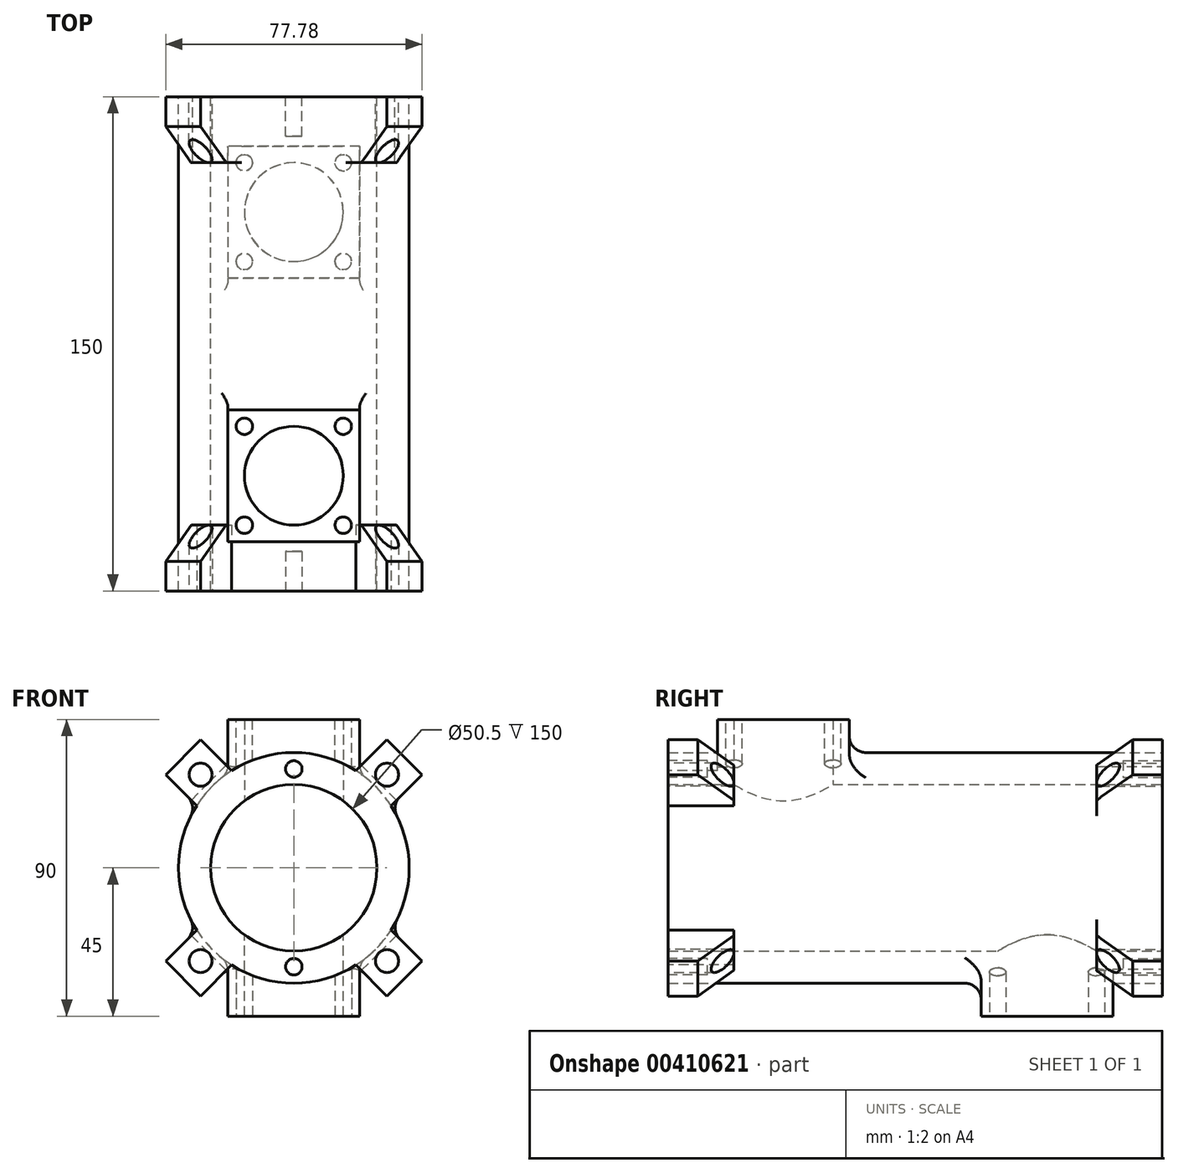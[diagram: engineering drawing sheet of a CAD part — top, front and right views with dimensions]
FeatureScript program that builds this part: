
annotation { "Feature Type Name" : "Feature", "Feature Type Description" : "" }
export const myFeature = defineFeature(function(context is Context, id is Id, definition is map)
    precondition{}
    {
        {
            var Q0;
            Q0=qCreatedBy(makeId("Front.planeOp"),FACE);
            var sketch = newSketch(context, id + "F0", { "sketchPlane" : qUnion([Q0])});
            skCircle(sketch, "E0", {"center": v(0, 0) * mm, "radius": 25.25 * mm});
            skCircle(sketch, "E1", {"center": v(0, 0) * mm, "radius": 35 * mm});
            skSolve(sketch);
        }
        {
            var Q0;
            Q0=makeQuery(id+"F0.imprint","IMPRINT",FACE,{"disambiguationData":[TD([[makeQuery(id+"F0.imprint","IMPRINT",EDGE,{"derivedFrom":sQuery(id+"F0.wireOp",EDGE,"E0")}),-1.0]])]});
            extrude(context, id + "F1", {"entities" : qUnion([Q0]), "depth" : 150 * mm});
        }
        {
            var Q0;
            Q0=qCreatedBy(makeId("Top.planeOp"),FACE);
            var sketch = newSketch(context, id + "F2", { "sketchPlane" : qUnion([Q0])});
            skCircle(sketch, "E2", {"center": v(0, -35) * mm, "radius": 15 * mm});
            skCircle(sketch, "E3", {"center": v(0, -115) * mm, "radius": 15 * mm});
            skSolve(sketch);
        }
        {
            var Q0;
            Q0=qCreatedBy(makeId("Top.planeOp"),FACE);
            cPlane(context, id + "F3", {"entities" : qUnion([Q0]), "cplaneType" : CPlaneType.OFFSET, "offset" : 45 * mm, "width" : 150 * mm, "height" : 150 * mm});
        }
        {
            var Q0;
            Q0=qCreatedBy(makeId("Top.planeOp"),FACE);
            cPlane(context, id + "F4", {"entities" : qUnion([Q0]), "cplaneType" : CPlaneType.OFFSET, "offset" : 45 * mm, "oppositeDirection" : true, "width" : 150 * mm, "height" : 150 * mm});
        }
        {
            var Q0;
            Q0=makeQuery(id+"F1.opExtrude","CAP_FACE",FACE,{"disambiguationData":[OSD([sQuery(id+"F0.wireOp",EDGE,"E0"),sQuery(id+"F0.wireOp",EDGE,"E1")])],"isStart":false});
            var sketch = newSketch(context, id + "F5", { "sketchPlane" : qUnion([Q0])});
            skLineSegment(sketch, "E4.bottom", {"start": v(-28.28, 17.68) * mm, "end": v(-38.9, 28.28) * mm});
            skLineSegment(sketch, "E4.top", {"start": v(-17.68, 28.28) * mm, "end": v(-28.28, 38.9) * mm});
            skLineSegment(sketch, "E4.left", {"start": v(-28.28, 17.68) * mm, "end": v(-17.68, 28.28) * mm});
            skLineSegment(sketch, "E4.right", {"start": v(-38.9, 28.28) * mm, "end": v(-28.28, 38.9) * mm});
            skPoint(sketch, "E4.middle", {"position": v(-28.28, 28.28) * mm});
            skLineSegment(sketch, "E5.bottom", {"start": v(28.28, 17.68) * mm, "end": v(17.68, 28.28) * mm});
            skLineSegment(sketch, "E5.top", {"start": v(38.9, 28.28) * mm, "end": v(28.28, 38.9) * mm});
            skLineSegment(sketch, "E5.left", {"start": v(28.28, 17.68) * mm, "end": v(38.9, 28.28) * mm});
            skLineSegment(sketch, "E5.right", {"start": v(17.68, 28.28) * mm, "end": v(28.28, 38.9) * mm});
            skPoint(sketch, "E5.middle", {"position": v(28.28, 28.28) * mm});
            skLineSegment(sketch, "E6.bottom", {"start": v(28.28, -38.9) * mm, "end": v(17.68, -28.28) * mm});
            skLineSegment(sketch, "E6.top", {"start": v(38.9, -28.28) * mm, "end": v(28.28, -17.68) * mm});
            skLineSegment(sketch, "E6.left", {"start": v(28.28, -38.9) * mm, "end": v(38.9, -28.28) * mm});
            skLineSegment(sketch, "E6.right", {"start": v(17.68, -28.28) * mm, "end": v(28.28, -17.68) * mm});
            skPoint(sketch, "E6.middle", {"position": v(28.28, -28.28) * mm});
            skLineSegment(sketch, "E7.bottom", {"start": v(-28.28, -38.9) * mm, "end": v(-38.9, -28.28) * mm});
            skLineSegment(sketch, "E7.top", {"start": v(-17.68, -28.28) * mm, "end": v(-28.28, -17.68) * mm});
            skLineSegment(sketch, "E7.left", {"start": v(-28.28, -38.9) * mm, "end": v(-17.68, -28.28) * mm});
            skLineSegment(sketch, "E7.right", {"start": v(-38.9, -28.28) * mm, "end": v(-28.28, -17.68) * mm});
            skPoint(sketch, "E7.middle", {"position": v(-28.28, -28.28) * mm});
            skCircle(sketch, "E8", {"center": v(0, 30) * mm, "radius": 2.5 * mm});
            skCircle(sketch, "E9", {"center": v(0, -30) * mm, "radius": 2.5 * mm});
            skCircle(sketch, "E10", {"center": v(28.28, 28.28) * mm, "radius": 3.5 * mm});
            skCircle(sketch, "E11", {"center": v(28.28, -28.28) * mm, "radius": 3.5 * mm});
            skCircle(sketch, "E12", {"center": v(-28.28, -28.28) * mm, "radius": 3.5 * mm});
            skCircle(sketch, "E13", {"center": v(-28.28, 28.28) * mm, "radius": 3.5 * mm});
            skLineSegment(sketch, "E14.0", {"start": v(-28.28, -38.9) * mm, "end": v(28.28, 17.68) * mm, "construction": true});
            skSolve(sketch);
        }
        {
            var Q0;
            Q0=makeQuery(id+"F1.opExtrude","CAP_FACE",FACE,{"disambiguationData":[OSD([sQuery(id+"F0.wireOp",EDGE,"E0"),sQuery(id+"F0.wireOp",EDGE,"E1")])],"isStart":true});
            var sketch = newSketch(context, id + "F6", { "sketchPlane" : qUnion([Q0])});
            skLineSegment(sketch, "E15.bottom", {"start": v(-28.28, 17.68) * mm, "end": v(-38.9, 28.28) * mm});
            skLineSegment(sketch, "E15.top", {"start": v(-17.68, 28.28) * mm, "end": v(-28.28, 38.9) * mm});
            skLineSegment(sketch, "E15.left", {"start": v(-28.28, 17.68) * mm, "end": v(-17.68, 28.28) * mm});
            skLineSegment(sketch, "E15.right", {"start": v(-38.9, 28.28) * mm, "end": v(-28.28, 38.9) * mm});
            skPoint(sketch, "E15.middle", {"position": v(-28.28, 28.28) * mm});
            skLineSegment(sketch, "E16.bottom", {"start": v(28.28, 17.68) * mm, "end": v(17.68, 28.28) * mm});
            skLineSegment(sketch, "E16.top", {"start": v(38.9, 28.28) * mm, "end": v(28.28, 38.9) * mm});
            skLineSegment(sketch, "E16.left", {"start": v(28.28, 17.68) * mm, "end": v(38.9, 28.28) * mm});
            skLineSegment(sketch, "E16.right", {"start": v(17.68, 28.28) * mm, "end": v(28.28, 38.9) * mm});
            skPoint(sketch, "E16.middle", {"position": v(28.28, 28.28) * mm});
            skLineSegment(sketch, "E17.bottom", {"start": v(28.28, -38.9) * mm, "end": v(17.68, -28.28) * mm});
            skLineSegment(sketch, "E17.top", {"start": v(38.9, -28.28) * mm, "end": v(28.28, -17.68) * mm});
            skLineSegment(sketch, "E17.left", {"start": v(28.28, -38.9) * mm, "end": v(38.9, -28.28) * mm});
            skLineSegment(sketch, "E17.right", {"start": v(17.68, -28.28) * mm, "end": v(28.28, -17.68) * mm});
            skPoint(sketch, "E17.middle", {"position": v(28.28, -28.28) * mm});
            skLineSegment(sketch, "E18.bottom", {"start": v(-28.28, -38.9) * mm, "end": v(-38.9, -28.28) * mm});
            skLineSegment(sketch, "E18.top", {"start": v(-17.68, -28.28) * mm, "end": v(-28.28, -17.68) * mm});
            skLineSegment(sketch, "E18.left", {"start": v(-28.28, -38.9) * mm, "end": v(-17.68, -28.28) * mm});
            skLineSegment(sketch, "E18.right", {"start": v(-38.9, -28.28) * mm, "end": v(-28.28, -17.68) * mm});
            skPoint(sketch, "E18.middle", {"position": v(-28.28, -28.28) * mm});
            skCircle(sketch, "E19", {"center": v(0, 30) * mm, "radius": 2.5 * mm});
            skCircle(sketch, "E20", {"center": v(0, -30) * mm, "radius": 2.5 * mm});
            skCircle(sketch, "E21", {"center": v(28.28, 28.28) * mm, "radius": 3.5 * mm});
            skCircle(sketch, "E22", {"center": v(28.28, -28.28) * mm, "radius": 3.5 * mm});
            skCircle(sketch, "E23", {"center": v(-28.28, -28.28) * mm, "radius": 3.5 * mm});
            skCircle(sketch, "E24", {"center": v(-28.28, 28.28) * mm, "radius": 3.5 * mm});
            skLineSegment(sketch, "E25.0", {"start": v(-28.28, -38.9) * mm, "end": v(28.28, 17.68) * mm, "construction": true});
            skSolve(sketch);
        }
        {
            var Q0;
            {var subQ0=sQuery(id+"F6.wireOp",EDGE,"E15.right");Q0=makeQuery(id+"F6.imprint","IMPRINT",FACE,{"disambiguationData":[TD([[makeQuery(id+"F6.imprint","IMPRINT",EDGE,{"derivedFrom":subQ0}),-1.0]])]});}
            var Q1;
            {var subQ1=sQuery(id+"F6.wireOp",EDGE,"E16.top");Q1=makeQuery(id+"F6.imprint","IMPRINT",FACE,{"disambiguationData":[TD([[makeQuery(id+"F6.imprint","IMPRINT",EDGE,{"derivedFrom":subQ1}),1.0]])]});}
            var Q2;
            {var subQ0=sQuery(id+"F6.wireOp",EDGE,"E17.left");Q2=makeQuery(id+"F6.imprint","IMPRINT",FACE,{"disambiguationData":[TD([[makeQuery(id+"F6.imprint","IMPRINT",EDGE,{"derivedFrom":subQ0}),1.0]])]});}
            var Q3;
            {var subQ1=sQuery(id+"F6.wireOp",EDGE,"E18.bottom");Q3=makeQuery(id+"F6.imprint","IMPRINT",FACE,{"disambiguationData":[TD([[makeQuery(id+"F6.imprint","IMPRINT",EDGE,{"derivedFrom":subQ1}),-1.0]])]});}
            var Q4;
            {var subQ0=sQuery(id+"F6.wireOp",EDGE,"E15.left");Q4=makeQuery(id+"F6.imprint","IMPRINT",FACE,{"disambiguationData":[TD([[makeQuery(id+"F6.imprint","IMPRINT",EDGE,{"derivedFrom":subQ0}),1.0]])]});}
            var Q5;
            {var subQ0=sQuery(id+"F6.wireOp",EDGE,"E16.bottom");Q5=makeQuery(id+"F6.imprint","IMPRINT",FACE,{"disambiguationData":[TD([[makeQuery(id+"F6.imprint","IMPRINT",EDGE,{"derivedFrom":subQ0}),-1.0]])]});}
            var Q6;
            {var subQ0=sQuery(id+"F6.wireOp",EDGE,"E18.top");Q6=makeQuery(id+"F6.imprint","IMPRINT",FACE,{"disambiguationData":[TD([[makeQuery(id+"F6.imprint","IMPRINT",EDGE,{"derivedFrom":subQ0}),1.0]])]});}
            var Q7;
            {var subQ0=sQuery(id+"F6.wireOp",EDGE,"E17.right");Q7=makeQuery(id+"F6.imprint","IMPRINT",FACE,{"disambiguationData":[TD([[makeQuery(id+"F6.imprint","IMPRINT",EDGE,{"derivedFrom":subQ0}),-1.0]])]});}
            extrude(context, id + "F7", {"entities" : qUnion([Q0, Q1, Q2, Q3, Q4, Q5, Q6, Q7]), "operationType" : NewBodyOperationType.ADD, "oppositeDirection" : true, "depth" : 20 * mm});
        }
        {
            var Q0;
            Q0=makeQuery(id+"F6.imprint","IMPRINT",FACE,{"disambiguationData":[TD([[makeQuery(id+"F6.imprint","IMPRINT",EDGE,{"derivedFrom":sQuery(id+"F6.wireOp",EDGE,"E19")}),1.0]])]});
            var Q1;
            Q1=makeQuery(id+"F6.imprint","IMPRINT",FACE,{"disambiguationData":[TD([[makeQuery(id+"F6.imprint","IMPRINT",EDGE,{"derivedFrom":sQuery(id+"F6.wireOp",EDGE,"E20")}),1.0]])]});
            var Q2;
            Q2=sQuery(id+"F6.wireOp",EDGE,"E19");
            var Q3;
            Q3=sQuery(id+"F6.wireOp",EDGE,"E20");
            extrude(context, id + "F8", {"entities" : qUnion([Q0, Q1]), "operationType" : NewBodyOperationType.REMOVE, "surfaceEntities" : qUnion([Q2, Q3]), "oppositeDirection" : true, "depth" : 12 * mm});
        }
        {
            var Q0;
            Q0=makeQuery(id+"F7.opExtrude","CAP_EDGE",EDGE,{"disambiguationData":[OSD([sQuery(id+"F6.wireOp",EDGE,"E15.right")])],"isStart":false});
            var Q1;
            Q1=makeQuery(id+"F7.opExtrude","CAP_EDGE",EDGE,{"disambiguationData":[OSD([sQuery(id+"F6.wireOp",EDGE,"E18.bottom")])],"isStart":false});
            var Q2;
            Q2=makeQuery(id+"F7.opExtrude","CAP_EDGE",EDGE,{"disambiguationData":[OSD([sQuery(id+"F6.wireOp",EDGE,"E16.top")])],"isStart":false});
            var Q3;
            Q3=makeQuery(id+"F7.opExtrude","CAP_EDGE",EDGE,{"disambiguationData":[OSD([sQuery(id+"F6.wireOp",EDGE,"E17.left")])],"isStart":false});
            chamfer(context, id + "F9", {"entities" : qUnion([Q0, Q1, Q2, Q3]), "width" : 11 * mm, "tangentPropagation" : true});
        }
        {
            var Q0;
            {var subQ0=sQuery(id+"F5.wireOp",EDGE,"E6.left");Q0=makeQuery(id+"F5.imprint","IMPRINT",FACE,{"disambiguationData":[TD([[makeQuery(id+"F5.imprint","IMPRINT",EDGE,{"derivedFrom":subQ0}),1.0]])]});}
            var Q1;
            {var subQ0=sQuery(id+"F5.wireOp",EDGE,"E7.bottom");Q1=makeQuery(id+"F5.imprint","IMPRINT",FACE,{"disambiguationData":[TD([[makeQuery(id+"F5.imprint","IMPRINT",EDGE,{"derivedFrom":subQ0}),-1.0]])]});}
            var Q2;
            {var subQ0=sQuery(id+"F5.wireOp",EDGE,"E4.right");Q2=makeQuery(id+"F5.imprint","IMPRINT",FACE,{"disambiguationData":[TD([[makeQuery(id+"F5.imprint","IMPRINT",EDGE,{"derivedFrom":subQ0}),-1.0]])]});}
            var Q3;
            {var subQ0=sQuery(id+"F5.wireOp",EDGE,"E5.top");Q3=makeQuery(id+"F5.imprint","IMPRINT",FACE,{"disambiguationData":[TD([[makeQuery(id+"F5.imprint","IMPRINT",EDGE,{"derivedFrom":subQ0}),1.0]])]});}
            extrude(context, id + "F10", {"entities" : qUnion([Q0, Q1, Q2, Q3]), "operationType" : NewBodyOperationType.ADD, "oppositeDirection" : true, "depth" : 20 * mm});
        }
        {
            var Q0;
            Q0=makeQuery(id+"F10.opExtrude","CAP_EDGE",EDGE,{"disambiguationData":[OSD([sQuery(id+"F5.wireOp",EDGE,"E4.right")])],"isStart":false});
            var Q1;
            Q1=makeQuery(id+"F10.opExtrude","CAP_EDGE",EDGE,{"disambiguationData":[OSD([sQuery(id+"F5.wireOp",EDGE,"E7.bottom")])],"isStart":false});
            var Q2;
            Q2=makeQuery(id+"F10.opExtrude","CAP_EDGE",EDGE,{"disambiguationData":[OSD([sQuery(id+"F5.wireOp",EDGE,"E6.left")])],"isStart":false});
            var Q3;
            Q3=makeQuery(id+"F10.opExtrude","CAP_EDGE",EDGE,{"disambiguationData":[OSD([sQuery(id+"F5.wireOp",EDGE,"E5.top")])],"isStart":false});
            chamfer(context, id + "F11", {"entities" : qUnion([Q0, Q1, Q2, Q3]), "width" : 11 * mm, "tangentPropagation" : true});
        }
        {
            var Q0;
            Q0=makeQuery(id+"F5.imprint","IMPRINT",FACE,{"disambiguationData":[TD([[makeQuery(id+"F5.imprint","IMPRINT",EDGE,{"derivedFrom":sQuery(id+"F5.wireOp",EDGE,"E8")}),1.0]])]});
            var Q1;
            Q1=makeQuery(id+"F5.imprint","IMPRINT",FACE,{"disambiguationData":[TD([[makeQuery(id+"F5.imprint","IMPRINT",EDGE,{"derivedFrom":sQuery(id+"F5.wireOp",EDGE,"E9")}),1.0]])]});
            var Q2;
            Q2=sQuery(id+"F5.wireOp",EDGE,"E8");
            var Q3;
            Q3=sQuery(id+"F5.wireOp",EDGE,"E9");
            extrude(context, id + "F12", {"entities" : qUnion([Q0, Q1]), "operationType" : NewBodyOperationType.REMOVE, "surfaceEntities" : qUnion([Q2, Q3]), "oppositeDirection" : true, "depth" : 12 * mm});
        }
        {
            var Q0;
            Q0=makeQuery(id+"F10.opExtrude","SWEPT_EDGE",EDGE,{"disambiguationData":[OSD([sQuery(id+"F0.wireOp",EDGE,"E1"),sQuery(id+"F5.wireOp",EDGE,"E6.bottom")])]});
            var Q1;
            Q1=makeQuery(id+"F10.opExtrude","SWEPT_EDGE",EDGE,{"disambiguationData":[OSD([sQuery(id+"F0.wireOp",EDGE,"E1"),sQuery(id+"F5.wireOp",EDGE,"E6.top")])]});
            var Q2;
            Q2=makeQuery(id+"F10.opExtrude","SWEPT_EDGE",EDGE,{"disambiguationData":[OSD([sQuery(id+"F0.wireOp",EDGE,"E1"),sQuery(id+"F5.wireOp",EDGE,"E5.left")])]});
            var Q3;
            Q3=makeQuery(id+"F10.opExtrude","SWEPT_EDGE",EDGE,{"disambiguationData":[OSD([sQuery(id+"F0.wireOp",EDGE,"E1"),sQuery(id+"F5.wireOp",EDGE,"E5.right")])]});
            var Q4;
            Q4=makeQuery(id+"F10.opExtrude","SWEPT_EDGE",EDGE,{"disambiguationData":[OSD([sQuery(id+"F0.wireOp",EDGE,"E1"),sQuery(id+"F5.wireOp",EDGE,"E4.top")])]});
            var Q5;
            Q5=makeQuery(id+"F10.opExtrude","SWEPT_EDGE",EDGE,{"disambiguationData":[OSD([sQuery(id+"F0.wireOp",EDGE,"E1"),sQuery(id+"F5.wireOp",EDGE,"E4.bottom")])]});
            var Q6;
            Q6=makeQuery(id+"F10.opExtrude","SWEPT_EDGE",EDGE,{"disambiguationData":[OSD([sQuery(id+"F0.wireOp",EDGE,"E1"),sQuery(id+"F5.wireOp",EDGE,"E7.right")])]});
            var Q7;
            Q7=makeQuery(id+"F10.opExtrude","SWEPT_EDGE",EDGE,{"disambiguationData":[OSD([sQuery(id+"F0.wireOp",EDGE,"E1"),sQuery(id+"F5.wireOp",EDGE,"E7.left")])]});
            var Q8;
            Q8=makeQuery(id+"F7.boolean.opBoolean","INTERSECT",EDGE,{"derivedFrom":[makeQuery(id+"F1.opExtrude","SWEPT_FACE",FACE,{"disambiguationData":[OSD([sQuery(id+"F0.wireOp",EDGE,"E1")])]}),makeQuery(id+"F7.opExtrude","SWEPT_FACE",FACE,{"disambiguationData":[OSD([sQuery(id+"F6.wireOp",EDGE,"E15.top")])]})]});
            var Q9;
            Q9=makeQuery(id+"F7.boolean.opBoolean","INTERSECT",EDGE,{"derivedFrom":[makeQuery(id+"F1.opExtrude","SWEPT_FACE",FACE,{"disambiguationData":[OSD([sQuery(id+"F0.wireOp",EDGE,"E1")])]}),makeQuery(id+"F7.opExtrude","SWEPT_FACE",FACE,{"disambiguationData":[OSD([sQuery(id+"F6.wireOp",EDGE,"E16.right")])]})]});
            var Q10;
            Q10=makeQuery(id+"F7.boolean.opBoolean","INTERSECT",EDGE,{"derivedFrom":[makeQuery(id+"F1.opExtrude","SWEPT_FACE",FACE,{"disambiguationData":[OSD([sQuery(id+"F0.wireOp",EDGE,"E1")])]}),makeQuery(id+"F7.opExtrude","SWEPT_FACE",FACE,{"disambiguationData":[OSD([sQuery(id+"F6.wireOp",EDGE,"E16.left")])]})]});
            var Q11;
            Q11=makeQuery(id+"F7.boolean.opBoolean","INTERSECT",EDGE,{"derivedFrom":[makeQuery(id+"F1.opExtrude","SWEPT_FACE",FACE,{"disambiguationData":[OSD([sQuery(id+"F0.wireOp",EDGE,"E1")])]}),makeQuery(id+"F7.opExtrude","SWEPT_FACE",FACE,{"disambiguationData":[OSD([sQuery(id+"F6.wireOp",EDGE,"E17.top")])]})]});
            var Q12;
            Q12=makeQuery(id+"F7.boolean.opBoolean","INTERSECT",EDGE,{"derivedFrom":[makeQuery(id+"F1.opExtrude","SWEPT_FACE",FACE,{"disambiguationData":[OSD([sQuery(id+"F0.wireOp",EDGE,"E1")])]}),makeQuery(id+"F7.opExtrude","SWEPT_FACE",FACE,{"disambiguationData":[OSD([sQuery(id+"F6.wireOp",EDGE,"E17.bottom")])]})]});
            var Q13;
            Q13=makeQuery(id+"F7.boolean.opBoolean","INTERSECT",EDGE,{"derivedFrom":[makeQuery(id+"F1.opExtrude","SWEPT_FACE",FACE,{"disambiguationData":[OSD([sQuery(id+"F0.wireOp",EDGE,"E1")])]}),makeQuery(id+"F7.opExtrude","SWEPT_FACE",FACE,{"disambiguationData":[OSD([sQuery(id+"F6.wireOp",EDGE,"E18.left")])]})]});
            var Q14;
            Q14=makeQuery(id+"F7.boolean.opBoolean","INTERSECT",EDGE,{"derivedFrom":[makeQuery(id+"F1.opExtrude","SWEPT_FACE",FACE,{"disambiguationData":[OSD([sQuery(id+"F0.wireOp",EDGE,"E1")])]}),makeQuery(id+"F7.opExtrude","SWEPT_FACE",FACE,{"disambiguationData":[OSD([sQuery(id+"F6.wireOp",EDGE,"E18.right")])]})]});
            var Q15;
            Q15=makeQuery(id+"F7.boolean.opBoolean","INTERSECT",EDGE,{"derivedFrom":[makeQuery(id+"F1.opExtrude","SWEPT_FACE",FACE,{"disambiguationData":[OSD([sQuery(id+"F0.wireOp",EDGE,"E1")])]}),makeQuery(id+"F7.opExtrude","SWEPT_FACE",FACE,{"disambiguationData":[OSD([sQuery(id+"F6.wireOp",EDGE,"E15.bottom")])]})]});
            fillet(context, id + "F13", {"entities" : qUnion([Q0, Q1, Q2, Q3, Q4, Q5, Q6, Q7, Q8, Q9, Q10, Q11, Q12, Q13, Q14, Q15]), "radius" : 5 * mm, "tangentPropagation" : true, "allowEdgeOverflow" : false});
        }
        {
            var Q0;
            Q0=qCreatedBy(id+"F3.planeOp",FACE);
            var sketch = newSketch(context, id + "F14", { "sketchPlane" : qUnion([Q0])});
            skLineSegment(sketch, "E26.bottom", {"start": v(20, -135) * mm, "end": v(-20, -135) * mm});
            skLineSegment(sketch, "E26.top", {"start": v(20, -95) * mm, "end": v(-20, -95) * mm});
            skLineSegment(sketch, "E26.left", {"start": v(20, -135) * mm, "end": v(20, -95) * mm});
            skLineSegment(sketch, "E26.right", {"start": v(-20, -135) * mm, "end": v(-20, -95) * mm});
            skPoint(sketch, "E26.middle", {"position": v(0, -115) * mm});
            skCircle(sketch, "E27", {"center": v(-15, -100) * mm, "radius": 2.5 * mm});
            skCircle(sketch, "E28", {"center": v(15, -100) * mm, "radius": 2.5 * mm});
            skCircle(sketch, "E29", {"center": v(15, -130) * mm, "radius": 2.5 * mm});
            skCircle(sketch, "E30", {"center": v(-15, -130) * mm, "radius": 2.5 * mm});
            skSolve(sketch);
        }
        {
            var Q0;
            Q0=makeQuery(id+"F14.imprint","IMPRINT",FACE,{"disambiguationData":[TD([[makeQuery(id+"F14.imprint","IMPRINT",EDGE,{"derivedFrom":sQuery(id+"F14.wireOp",EDGE,"E26.bottom")}),-1.0]])]});
            extrude(context, id + "F15", {"entities" : qUnion([Q0]), "operationType" : NewBodyOperationType.ADD, "oppositeDirection" : true, "depth" : 18.5 * mm});
        }
        {
            var Q0;
            Q0=makeQuery(id+"F2.imprint","IMPRINT",FACE,{"disambiguationData":[TD([[makeQuery(id+"F2.imprint","IMPRINT",EDGE,{"derivedFrom":sQuery(id+"F2.wireOp",EDGE,"E3")}),1.0]])]});
            extrude(context, id + "F16", {"entities" : qUnion([Q0]), "operationType" : NewBodyOperationType.REMOVE, "depth" : 47.4 * mm});
        }
        {
            var Q0;
            Q0=qCreatedBy(id+"F4.planeOp",FACE);
            var sketch = newSketch(context, id + "F17", { "sketchPlane" : qUnion([Q0])});
            skLineSegment(sketch, "E31.bottom", {"start": v(20, -15) * mm, "end": v(-20, -15) * mm});
            skLineSegment(sketch, "E31.top", {"start": v(20, -55) * mm, "end": v(-20, -55) * mm});
            skLineSegment(sketch, "E31.left", {"start": v(20, -15) * mm, "end": v(20, -55) * mm});
            skLineSegment(sketch, "E31.right", {"start": v(-20, -15) * mm, "end": v(-20, -55) * mm});
            skPoint(sketch, "E31.middle", {"position": v(0, -35) * mm});
            skCircle(sketch, "E32", {"center": v(-15, -50) * mm, "radius": 2.5 * mm});
            skCircle(sketch, "E33", {"center": v(15, -50) * mm, "radius": 2.5 * mm});
            skCircle(sketch, "E34", {"center": v(15, -20) * mm, "radius": 2.5 * mm});
            skCircle(sketch, "E35", {"center": v(-15, -20) * mm, "radius": 2.5 * mm});
            skSolve(sketch);
        }
        {
            var Q0;
            Q0=makeQuery(id+"F17.imprint","IMPRINT",FACE,{"disambiguationData":[TD([[makeQuery(id+"F17.imprint","IMPRINT",EDGE,{"derivedFrom":sQuery(id+"F17.wireOp",EDGE,"E31.bottom")}),1.0]])]});
            extrude(context, id + "F18", {"entities" : qUnion([Q0]), "operationType" : NewBodyOperationType.ADD, "depth" : 18.5 * mm});
        }
        {
            var Q0;
            Q0=makeQuery(id+"F2.imprint","IMPRINT",FACE,{"disambiguationData":[TD([[makeQuery(id+"F2.imprint","IMPRINT",EDGE,{"derivedFrom":sQuery(id+"F2.wireOp",EDGE,"E2")}),1.0]])]});
            var Q1;
            Q1=sQuery(id+"F2.wireOp",EDGE,"E2");
            extrude(context, id + "F19", {"entities" : qUnion([Q0]), "operationType" : NewBodyOperationType.REMOVE, "surfaceEntities" : qUnion([Q1]), "oppositeDirection" : true, "depth" : 54 * mm});
        }
        {
            var Q0;
            {var subQ1=sQuery(id+"F0.wireOp",EDGE,"E1");Q0=makeQuery(id+"F18.boolean.opBoolean","INTERSECT",EDGE,{"derivedFrom":[makeQuery(id+"F15.boolean.opBoolean","SPLIT",FACE,{"disambiguationData":[TD([makeQuery(id+"F15.opExtrude","SWEPT_FACE",FACE,{"disambiguationData":[OSD([sQuery(id+"F14.wireOp",EDGE,"E26.top")])]})])],"derivedFrom":makeQuery(id+"F1.opExtrude","SWEPT_FACE",FACE,{"disambiguationData":[OSD([subQ1])]})}),makeQuery(id+"F18.opExtrude","SWEPT_FACE",FACE,{"disambiguationData":[OSD([sQuery(id+"F17.wireOp",EDGE,"E31.left")])]})]});}
            var Q1;
            {var subQ1=sQuery(id+"F0.wireOp",EDGE,"E1");Q1=makeQuery(id+"F18.boolean.opBoolean","INTERSECT",EDGE,{"derivedFrom":[makeQuery(id+"F15.boolean.opBoolean","SPLIT",FACE,{"disambiguationData":[TD([makeQuery(id+"F15.opExtrude","SWEPT_FACE",FACE,{"disambiguationData":[OSD([sQuery(id+"F14.wireOp",EDGE,"E26.top")])]})])],"derivedFrom":makeQuery(id+"F1.opExtrude","SWEPT_FACE",FACE,{"disambiguationData":[OSD([subQ1])]})}),makeQuery(id+"F18.opExtrude","SWEPT_FACE",FACE,{"disambiguationData":[OSD([sQuery(id+"F17.wireOp",EDGE,"E31.right")])]})]});}
            var Q2;
            Q2=makeQuery(id+"F15.boolean.opBoolean","INTERSECT",EDGE,{"derivedFrom":[makeQuery(id+"F1.opExtrude","SWEPT_FACE",FACE,{"disambiguationData":[OSD([sQuery(id+"F0.wireOp",EDGE,"E1")])]}),makeQuery(id+"F15.opExtrude","SWEPT_FACE",FACE,{"disambiguationData":[OSD([sQuery(id+"F14.wireOp",EDGE,"E26.top")])]})]});
            var Q3;
            Q3=makeQuery(id+"F15.boolean.opBoolean","INTERSECT",EDGE,{"derivedFrom":[makeQuery(id+"F1.opExtrude","SWEPT_FACE",FACE,{"disambiguationData":[OSD([sQuery(id+"F0.wireOp",EDGE,"E1")])]}),makeQuery(id+"F15.opExtrude","SWEPT_FACE",FACE,{"disambiguationData":[OSD([sQuery(id+"F14.wireOp",EDGE,"E26.right")])]})]});
            var Q4;
            Q4=makeQuery(id+"F15.boolean.opBoolean","INTERSECT",EDGE,{"derivedFrom":[makeQuery(id+"F1.opExtrude","SWEPT_FACE",FACE,{"disambiguationData":[OSD([sQuery(id+"F0.wireOp",EDGE,"E1")])]}),makeQuery(id+"F15.opExtrude","SWEPT_FACE",FACE,{"disambiguationData":[OSD([sQuery(id+"F14.wireOp",EDGE,"E26.left")])]})]});
            var Q5;
            {var subQ1=sQuery(id+"F0.wireOp",EDGE,"E1");Q5=makeQuery(id+"F18.boolean.opBoolean","INTERSECT",EDGE,{"derivedFrom":[makeQuery(id+"F15.boolean.opBoolean","SPLIT",FACE,{"disambiguationData":[TD([makeQuery(id+"F15.opExtrude","SWEPT_FACE",FACE,{"disambiguationData":[OSD([sQuery(id+"F14.wireOp",EDGE,"E26.top")])]})])],"derivedFrom":makeQuery(id+"F1.opExtrude","SWEPT_FACE",FACE,{"disambiguationData":[OSD([subQ1])]})}),makeQuery(id+"F18.opExtrude","SWEPT_FACE",FACE,{"disambiguationData":[OSD([sQuery(id+"F17.wireOp",EDGE,"E31.top")])]})]});}
            fillet(context, id + "F20", {"entities" : qUnion([Q0, Q1, Q2, Q3, Q4, Q5]), "radius" : 5 * mm, "tangentPropagation" : true, "allowEdgeOverflow" : false});
        }
        {
            var Q0;
            Q0=makeQuery(id+"F14.imprint","IMPRINT",FACE,{"disambiguationData":[TD([[makeQuery(id+"F14.imprint","IMPRINT",EDGE,{"derivedFrom":sQuery(id+"F14.wireOp",EDGE,"E28")}),1.0]])]});
            var Q1;
            Q1=makeQuery(id+"F14.imprint","IMPRINT",FACE,{"disambiguationData":[TD([[makeQuery(id+"F14.imprint","IMPRINT",EDGE,{"derivedFrom":sQuery(id+"F14.wireOp",EDGE,"E27")}),1.0]])]});
            var Q2;
            Q2=makeQuery(id+"F14.imprint","IMPRINT",FACE,{"disambiguationData":[TD([[makeQuery(id+"F14.imprint","IMPRINT",EDGE,{"derivedFrom":sQuery(id+"F14.wireOp",EDGE,"E30")}),1.0]])]});
            var Q3;
            Q3=makeQuery(id+"F14.imprint","IMPRINT",FACE,{"disambiguationData":[TD([[makeQuery(id+"F14.imprint","IMPRINT",EDGE,{"derivedFrom":sQuery(id+"F14.wireOp",EDGE,"E29")}),1.0]])]});
            extrude(context, id + "F21", {"entities" : qUnion([Q0, Q1, Q2, Q3]), "operationType" : NewBodyOperationType.REMOVE, "oppositeDirection" : true, "depth" : 8 * mm});
        }
    });
